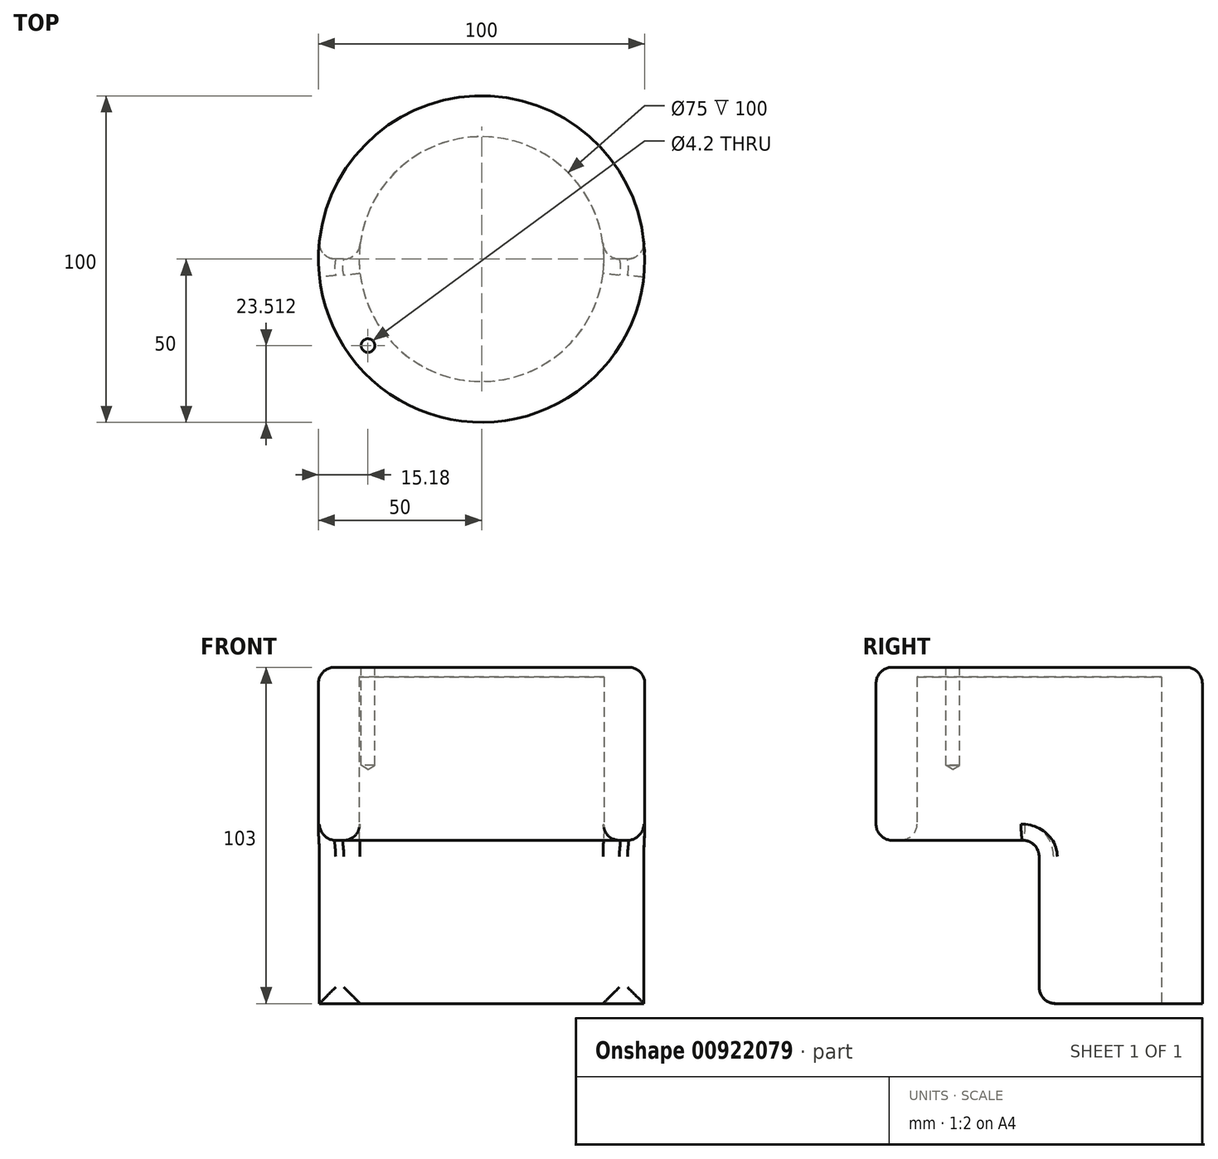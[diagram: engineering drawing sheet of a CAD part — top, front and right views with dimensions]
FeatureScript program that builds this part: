
annotation { "Feature Type Name" : "Feature", "Feature Type Description" : "" }
export const myFeature = defineFeature(function(context is Context, id is Id, definition is map)
    precondition{}
    {
        {
            var Q0;
            Q0=qCreatedBy(makeId("Top.planeOp"),FACE);
            var sketch = newSketch(context, id + "F0", { "sketchPlane" : qUnion([Q0])});
            skCircle(sketch, "E0", {"center": v(0, 0) * mm, "radius": 50 * mm});
            skCircle(sketch, "E1", {"center": v(0, 0) * mm, "radius": 37.5 * mm});
            skSolve(sketch);
        }
        {
            var Q0;
            Q0 = qSketchRegion(id + "F0", true);
            extrude(context, id + "F1", {"entities" : qUnion([Q0]), "depth" : 100 * mm, "offsetDistance" : 25 * mm});
        }
        {
            var Q0;
            Q0=qCreatedBy(makeId("Front.planeOp"),FACE);
            var sketch = newSketch(context, id + "F2", { "sketchPlane" : qUnion([Q0])});
            skLineSegment(sketch, "E2.bottom", {"start": v(173.64, 0) * mm, "end": v(-170.39, 0) * mm});
            skLineSegment(sketch, "E2.top", {"start": v(173.64, 50) * mm, "end": v(-170.39, 50) * mm});
            skLineSegment(sketch, "E2.left", {"start": v(173.64, 0) * mm, "end": v(173.64, 50) * mm});
            skLineSegment(sketch, "E2.right", {"start": v(-170.39, 0) * mm, "end": v(-170.39, 50) * mm});
            skSolve(sketch);
        }
        {
            var Q0;
            Q0 = qSketchRegion(id + "F2", true);
            extrude(context, id + "F3", {"entities" : qUnion([Q0]), "operationType" : NewBodyOperationType.REMOVE, "endBound" : BoundingType.THROUGH_ALL, "depth" : 25 * mm, "offsetDistance" : 25 * mm});
        }
        {
            var Q0;
            Q0=makeQuery(id+"F1.opExtrude","CAP_FACE",FACE,{"disambiguationData":[OSD([sQuery(id+"F0.wireOp",EDGE,"E0"),sQuery(id+"F0.wireOp",EDGE,"E1")])],"isStart":false});
            var sketch = newSketch(context, id + "F4", { "sketchPlane" : qUnion([Q0])});
            skCircle(sketch, "E3", {"center": v(0, 0) * mm, "radius": 50 * mm});
            skSolve(sketch);
        }
        {
            var Q0;
            Q0 = qSketchRegion(id + "F4", true);
            extrude(context, id + "F5", {"entities" : qUnion([Q0]), "operationType" : NewBodyOperationType.ADD, "depth" : 3 * mm, "offsetDistance" : 25 * mm});
        }
        {
            var Q0;
            Q0=makeQuery(id+"F3.boolean.opBoolean","INTERSECT",EDGE,{"derivedFrom":[makeQuery(id+"F1.opExtrude","SWEPT_FACE",FACE,{"disambiguationData":[OSD([sQuery(id+"F0.wireOp",EDGE,"E0")])]}),makeQuery(id+"F3.opExtrude","SWEPT_FACE",FACE,{"disambiguationData":[OSD([sQuery(id+"F2.wireOp",EDGE,"E2.top")])]})]});
            var Q1;
            Q1=makeQuery(id+"F3.boolean.opBoolean","INTERSECT",EDGE,{"derivedFrom":[makeQuery(id+"F1.opExtrude","SWEPT_FACE",FACE,{"disambiguationData":[OSD([sQuery(id+"F0.wireOp",EDGE,"E1")])]}),makeQuery(id+"F3.opExtrude","SWEPT_FACE",FACE,{"disambiguationData":[OSD([sQuery(id+"F2.wireOp",EDGE,"E2.top")])]})]});
            var Q2;
            Q2=makeQuery(id+"F5.opExtrude","CAP_EDGE",EDGE,{"disambiguationData":[OSD([sQuery(id+"F4.wireOp",EDGE,"E3")])],"isStart":false});
            var Q3;
            Q3=makeQuery(id+"F3.boolean.opBoolean","COPY",FACE,{"disambiguationData":[OD(0.0)],"derivedFrom":makeQuery(id+"F3.opExtrude","CAP_FACE",FACE,{"disambiguationData":[OSD([sQuery(id+"F2.wireOp",EDGE,"E2.bottom"),sQuery(id+"F2.wireOp",EDGE,"E2.top"),sQuery(id+"F2.wireOp",EDGE,"E2.left"),sQuery(id+"F2.wireOp",EDGE,"E2.right")])],"isStart":true})});
            var Q4;
            Q4=makeQuery(id+"F3.boolean.opBoolean","COPY",FACE,{"disambiguationData":[OD(1.0)],"derivedFrom":makeQuery(id+"F3.opExtrude","CAP_FACE",FACE,{"disambiguationData":[OSD([sQuery(id+"F2.wireOp",EDGE,"E2.bottom"),sQuery(id+"F2.wireOp",EDGE,"E2.top"),sQuery(id+"F2.wireOp",EDGE,"E2.left"),sQuery(id+"F2.wireOp",EDGE,"E2.right")])],"isStart":true})});
            fillet(context, id + "F6", {"entities" : qUnion([Q0, Q1, Q2, Q3, Q4]), "radius" : 5 * mm, "tangentPropagation" : true, "allowEdgeOverflow" : false});
        }
        {
            var Q0;
            Q0=makeQuery(id+"F5.opExtrude","CAP_FACE",FACE,{"disambiguationData":[OSD([sQuery(id+"F4.wireOp",EDGE,"E3")])],"isStart":false});
            var sketch = newSketch(context, id + "F7", { "sketchPlane" : qUnion([Q0])});
            skCircle(sketch, "E4", {"center": v(0, 0) * mm, "radius": 43.75 * mm});
            skPoint(sketch, "E5", {"position": v(-34.82, -26.49) * mm});
            skSolve(sketch);
        }
        {
            var Q0;
            Q0=sQuery(id+"F7.wireOp",VERTEX,"E5");
            var Q1;
            Q1=makeQuery(id+"F1.opExtrude","SWEPT_BODY",BODY,{"disambiguationData":[OSD([sQuery(id+"F0.wireOp",EDGE,"E0"),sQuery(id+"F0.wireOp",EDGE,"E1")])]});
            hole(context, id + "F8", {"style" : HoleStyle.SIMPLE, "endStyle" : HoleEndStyle.BLIND, "standardTappedOrClearance" : lookupTablePath({ "standard" : "ISO", "engagement" : "75%", "pitch" : "0.8 mm", "size" : "M5", "type" : "Tapped" }), "standardBlindInLast" : lookupTablePath({ "standard" : "ISO", "engagement" : "75%", "pitch" : "0.8 mm", "size" : "M5", "type" : "Tapped" }), "holeDiameter" : 4.2 * mm, "majorDiameter" : 5 * mm, "showTappedDepth" : true, "holeDepth" : 30 * mm, "isTappedThrough" : true, "tappedDepth" : 27.6 * mm, "tapClearance" : 3, "locations" : qUnion([Q0]), "scope" : qUnion([Q1])});
        }
    });
